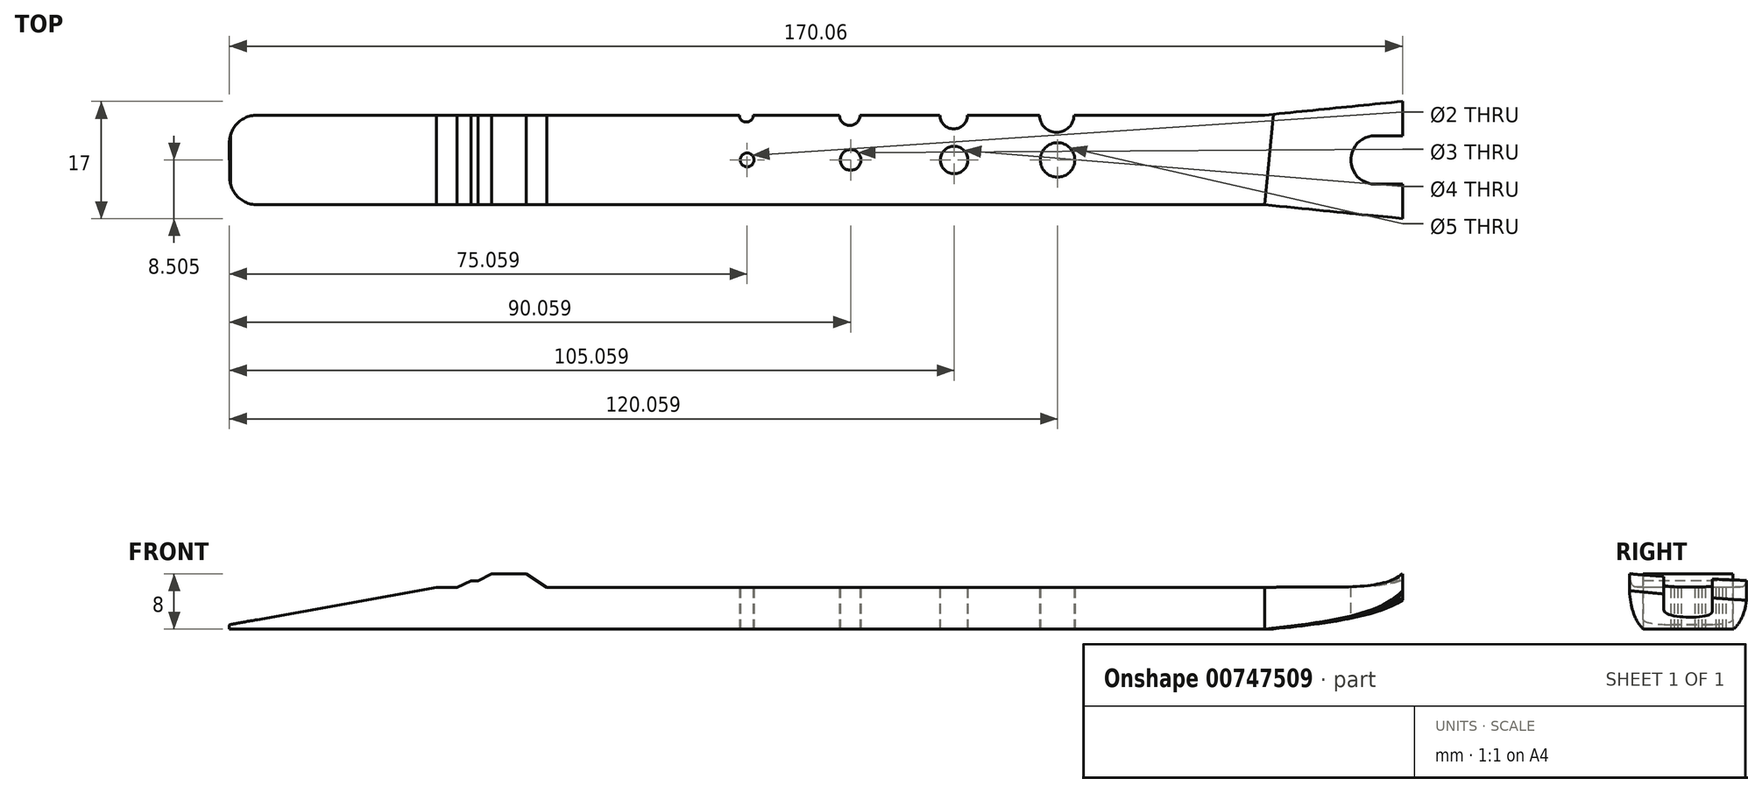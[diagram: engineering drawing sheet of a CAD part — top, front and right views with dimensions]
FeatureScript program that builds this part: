
annotation { "Feature Type Name" : "Feature", "Feature Type Description" : "" }
export const myFeature = defineFeature(function(context is Context, id is Id, definition is map)
    precondition{}
    {
        {
            var Q0;
            Q0=qCreatedBy(makeId("Top.planeOp"),FACE);
            var sketch = newSketch(context, id + "F0", { "sketchPlane" : qUnion([Q0])});
            skLineSegment(sketch, "E0", {"start": v(-98.1, -25.9) * mm, "end": v(47.93, -25.9) * mm});
            skLineSegment(sketch, "E1", {"start": v(47.93, -25.9) * mm, "end": v(47.93, -12.9) * mm});
            skLineSegment(sketch, "E2", {"start": v(47.93, -12.9) * mm, "end": v(20.3, -12.9) * mm});
            skCircle(sketch, "E3", {"center": v(-27.07, -19.4) * mm, "radius": 1 * mm});
            skCircle(sketch, "E4", {"center": v(-12.07, -19.4) * mm, "radius": 1.5 * mm});
            skCircle(sketch, "E5", {"center": v(2.93, -19.4) * mm, "radius": 2 * mm});
            skCircle(sketch, "E6", {"center": v(17.93, -19.4) * mm, "radius": 2.5 * mm});
            skArc(sketch, "E7", {"start": v(-28.2, -12.9) * mm, "mid": v(-27.2, -13.9) * mm, "end": v(-26.2, -12.9) * mm});
            skArc(sketch, "E8", {"start": v(-13.7, -12.9) * mm, "mid": v(-12.2, -14.4) * mm, "end": v(-10.7, -12.9) * mm});
            skArc(sketch, "E9", {"start": v(0.87, -12.9) * mm, "mid": v(2.87, -14.9) * mm, "end": v(4.87, -12.9) * mm});
            skArc(sketch, "E10", {"start": v(15.3, -12.9) * mm, "mid": v(17.8, -15.4) * mm, "end": v(20.3, -12.9) * mm});
            skLineSegment(sketch, "E11.trimOffspring", {"start": v(-28.2, -12.9) * mm, "end": v(-42.2, -12.9) * mm});
            skLineSegment(sketch, "E12.trimOffspring", {"start": v(-13.7, -12.9) * mm, "end": v(-26.2, -12.9) * mm});
            skLineSegment(sketch, "E13.trimOffspring", {"start": v(0.87, -12.9) * mm, "end": v(-10.7, -12.9) * mm});
            skLineSegment(sketch, "E14.trimOffspring", {"start": v(15.3, -12.9) * mm, "end": v(4.87, -12.9) * mm});
            skLineSegment(sketch, "E15", {"start": v(-42.2, -12.9) * mm, "end": v(-98.13, -12.9) * mm});
            skLineSegment(sketch, "E16", {"start": v(-42.2, -12.9) * mm, "end": v(-42.2, -25.9) * mm});
            skLineSegment(sketch, "E17", {"start": v(-102.13, -16.92) * mm, "end": v(-102.1, -21.92) * mm});
            skLineSegment(sketch, "E18", {"start": v(17.93, -19.4) * mm, "end": v(17.93, -25.9) * mm});
            skPoint(sketch, "E19.visualSharp", {"position": v(-102.16, -12.9) * mm});
            skArc(sketch, "E19.filletArc", {"start": v(-98.13, -12.9) * mm, "mid": v(-100.97, -14.07) * mm, "end": v(-102.13, -16.92) * mm});
            skPoint(sketch, "E20.visualSharp", {"position": v(-102.09, -25.9) * mm});
            skArc(sketch, "E20.filletArc", {"start": v(-102.1, -21.92) * mm, "mid": v(-100.93, -24.73) * mm, "end": v(-98.1, -25.9) * mm});
            skSolve(sketch);
        }
        {
            var Q0;
            {var subQ3=sQuery(id+"F0.wireOp",EDGE,"E1");Q0=makeQuery(id+"F0.imprint","IMPRINT",FACE,{"disambiguationData":[TD([[makeQuery(id+"F0.imprint","IMPRINT",EDGE,{"derivedFrom":subQ3}),1.0]])]});}
            var Q1;
            Q1=makeQuery(id+"F0.imprint","IMPRINT",FACE,{"disambiguationData":[TD([[makeQuery(id+"F0.imprint","IMPRINT",EDGE,{"derivedFrom":sQuery(id+"F0.wireOp",EDGE,"E15")}),1.0]])]});
            var Q2;
            Q2 = qSketchRegion(id + "F2", true);
            extrude(context, id + "F1", {"entities" : qUnion([Q0, Q1, Q2]), "depth" : 6 * mm, "offsetDistance" : 25 * mm});
        }
        {
            var Q0;
            Q0=makeQuery(id+"F1.opExtrude","CAP_FACE",FACE,{"disambiguationData":[OSD([sQuery(id+"F0.wireOp",EDGE,"uh8EjRIv-oyds-LonH-DEWT-FKtuM7sv1xbY"),sQuery(id+"F0.wireOp",EDGE,"2pE5EAkt-IuKl-0Sab-UQfI-aqEs6KhZttEm"),sQuery(id+"F0.wireOp",EDGE,"Nk6HZn5N-y9iB-Nk6B-fPmU-OZDAcxOevotu"),sQuery(id+"F0.wireOp",EDGE,"LXX49E4n-5PRi-B9FO-bH7N-pa6ycjuBgqBC"),sQuery(id+"F0.wireOp",EDGE,"53KMTElE-K7W9-ORrf-RCAp-qNT4eaaVkteF"),sQuery(id+"F0.wireOp",EDGE,"P7PF4Mbg-ef0C-n9oX-XZ09-ZLFXLgH8y7fW"),sQuery(id+"F0.wireOp",EDGE,"su197C0L-hHtV-Jca1-MSLm-PElzWjnIUR3Y"),sQuery(id+"F0.wireOp",EDGE,"EV9Pacv8-165I-bCM3-OcYT-9LR3dg5SSEyu"),sQuery(id+"F0.wireOp",EDGE,"19IYVO1Q-Y4kt-bx1a-DxFm-OXG8GlXLaGFM"),sQuery(id+"F0.wireOp",EDGE,"65VxX6mh-rfcX-KxfM-GORW-ms9ADtBnMzlR"),sQuery(id+"F0.wireOp",EDGE,"7bQUvBXv-wM8X-eBwg-Mk0h-ePabGQXhmWVm"),sQuery(id+"F0.wireOp",EDGE,"bDx1VqJG-FhMZ-ysIe-255i-NBJnI1b9v1Xd"),sQuery(id+"F0.wireOp",EDGE,"GWuhjFGg-mN8e-GpBZ-US7o-J5IPN2826qVD"),sQuery(id+"F0.wireOp",EDGE,"91LzrW2M-BcOK-ah0N-KhqT-TaDJfhBesgPh"),sQuery(id+"F0.wireOp",EDGE,"1k80qitz-qzns-NigU-Vkyj-1TzsJOIY6Jo9"),sQuery(id+"F0.wireOp",EDGE,"p5sEo6Ta-pkgy-Fa4L-bMfm-GfEhippCeM6v"),sQuery(id+"F0.wireOp",EDGE,"VcT0GBPq-V1kq-JeiP-DT5O-q3OzsVNUBB7H"),sQuery(id+"F0.wireOp",EDGE,"vWu1ZsAQ-pDto-N3AH-TT21-yHdSeIgjR8fg"),sQuery(id+"F0.wireOp",EDGE,"vBJXVKXv-qYgn-2ukd-IsI3-EiIpIBPK8Vaz"),sQuery(id+"F0.wireOp",EDGE,"G37NeImH-WY8i-Es2l-a97g-44kHUUvCxSSy"),sQuery(id+"F0.wireOp",EDGE,"E7LrDzYy-OpsH-mPZP-qLcD-qzzZRt0giBqK"),sQuery(id+"F0.wireOp",EDGE,"s3JVjWtr-fkdu-SgC5-uSSM-x588ayeuHTqY"),sQuery(id+"F0.wireOp",EDGE,"Z1yXTLh1-1L1P-RAfO-bNF2-wSMogvR3wL57"),sQuery(id+"F0.wireOp",EDGE,"ZUVO2fO2-Q0JX-bRAt-EWbK-FMEUTOadSTGL"),sQuery(id+"F0.wireOp",EDGE,"OpzXb7L7-065u-pUx9-msa7-Or2I1k12Jhel"),sQuery(id+"F0.wireOp",EDGE,"E0"),sQuery(id+"F0.wireOp",EDGE,"E1"),sQuery(id+"F0.wireOp",EDGE,"E2"),sQuery(id+"F0.wireOp",EDGE,"E3"),sQuery(id+"F0.wireOp",EDGE,"E4"),sQuery(id+"F0.wireOp",EDGE,"E5"),sQuery(id+"F0.wireOp",EDGE,"E6"),sQuery(id+"F0.wireOp",EDGE,"E7"),sQuery(id+"F0.wireOp",EDGE,"E8"),sQuery(id+"F0.wireOp",EDGE,"E9"),sQuery(id+"F0.wireOp",EDGE,"E10"),sQuery(id+"F0.wireOp",EDGE,"E11.trimOffspring"),sQuery(id+"F0.wireOp",EDGE,"E12.trimOffspring"),sQuery(id+"F0.wireOp",EDGE,"E13.trimOffspring"),sQuery(id+"F0.wireOp",EDGE,"E14.trimOffspring")])],"isStart":true});
            var sketch = newSketch(context, id + "F2", { "sketchPlane" : qUnion([Q0])});
            skLineSegment(sketch, "E21", {"start": v(47.93, 12.9) * mm, "end": v(47.93, 25.9) * mm});
            skLineSegment(sketch, "E22", {"start": v(47.93, 25.9) * mm, "end": v(67.93, 27.9) * mm});
            skLineSegment(sketch, "E23", {"start": v(47.93, 12.9) * mm, "end": v(67.93, 10.9) * mm});
            skLineSegment(sketch, "E24", {"start": v(67.93, 27.9) * mm, "end": v(67.93, 22.9) * mm});
            skLineSegment(sketch, "E25", {"start": v(67.93, 10.9) * mm, "end": v(67.93, 15.9) * mm});
            skLineSegment(sketch, "E26", {"start": v(67.93, 15.9) * mm, "end": v(63.93, 15.9) * mm});
            skLineSegment(sketch, "E27", {"start": v(67.93, 22.9) * mm, "end": v(63.93, 22.9) * mm});
            skArc(sketch, "E28", {"start": v(63.93, 15.9) * mm, "mid": v(60.43, 19.4) * mm, "end": v(63.93, 22.9) * mm});
            skSolve(sketch);
        }
        {
            var Q0;
            Q0=makeQuery(id+"F2.imprint","IMPRINT",FACE,{"disambiguationData":[TD([[makeQuery(id+"F2.imprint","IMPRINT",EDGE,{"derivedFrom":sQuery(id+"F2.wireOp",EDGE,"E21")}),1.0]])]});
            extrude(context, id + "F3", {"entities" : qUnion([Q0]), "operationType" : NewBodyOperationType.ADD, "oppositeDirection" : true, "depth" : 8 * mm, "offsetDistance" : 25 * mm});
        }
        {
            var Q0;
            Q0=makeQuery(id+"F3.opExtrude","SWEPT_FACE",FACE,{"disambiguationData":[OSD([sQuery(id+"F2.wireOp",EDGE,"E22")])]});
            var sketch = newSketch(context, id + "F4", { "sketchPlane" : qUnion([Q0])});
            skFitSpline(sketch, "E29", {"points": [v(50.27, 6) * mm, v(70.37, 8) * mm, v(72.3, 17.02) * mm], "startDerivative": vector(42.2, 1.96) * mm, "endDerivative": vector(-0.97, 25.63) * mm});
            skFitSpline(sketch, "E30", {"points": [v(50.27, 0) * mm, v(70.37, 5.57) * mm, v(72.3, 17.02) * mm], "startDerivative": vector(43.85, 4.84) * mm, "endDerivative": vector(-2.02, 30.43) * mm});
            skLineSegment(sketch, "E31", {"start": v(50.27, 21.53) * mm, "end": v(74.87, 21.53) * mm});
            skLineSegment(sketch, "E32", {"start": v(74.87, 21.53) * mm, "end": v(74.87, -3.93) * mm});
            skLineSegment(sketch, "E33", {"start": v(74.87, -3.93) * mm, "end": v(50.27, -3.93) * mm});
            skLineSegment(sketch, "E34", {"start": v(50.27, -3.93) * mm, "end": v(50.27, 0) * mm});
            skLineSegment(sketch, "E35", {"start": v(50.27, 6) * mm, "end": v(47.71, 6) * mm});
            skLineSegment(sketch, "E36", {"start": v(47.71, 6) * mm, "end": v(47.71, 21.53) * mm});
            skLineSegment(sketch, "E37", {"start": v(47.71, 21.53) * mm, "end": v(50.27, 21.53) * mm});
            skSolve(sketch);
        }
        {
            var Q0;
            Q0=makeQuery(id+"F4.imprint","IMPRINT",FACE,{"disambiguationData":[TD([[makeQuery(id+"F4.imprint","IMPRINT",EDGE,{"derivedFrom":sQuery(id+"F4.wireOp",EDGE,"E31")}),-1.0]])]});
            var Q1;
            {var subQ1=sQuery(id+"F2.wireOp",EDGE,"E22");var subQ2=makeQuery(id+"F3.opExtrude","CAP_EDGE",EDGE,{"disambiguationData":[OSD([subQ1])],"isStart":false});Q1=makeQuery(id+"F4.imprint","IMPRINT",FACE,{"disambiguationData":[TD([[makeQuery(id+"F4.imprint","IMPRINT",EDGE,{"derivedFrom":subQ2}),-1.0]])]});}
            var Q2;
            {var subQ1=sQuery(id+"F2.wireOp",EDGE,"E22");var subQ3=makeQuery(id+"F3.opExtrude","CAP_EDGE",EDGE,{"disambiguationData":[OSD([subQ1])],"isStart":true});Q2=makeQuery(id+"F4.imprint","IMPRINT",FACE,{"disambiguationData":[TD([[makeQuery(id+"F4.imprint","IMPRINT",EDGE,{"derivedFrom":subQ3}),1.0]])]});}
            extrude(context, id + "F5", {"entities" : qUnion([Q0, Q1, Q2]), "operationType" : NewBodyOperationType.REMOVE, "oppositeDirection" : true, "depth" : 25 * mm, "offsetDistance" : 25 * mm});
        }
        {
            var Q0;
            Q0=makeQuery(id+"F1.opExtrude","SWEPT_FACE",FACE,{"disambiguationData":[OSD([sQuery(id+"F0.wireOp",EDGE,"E0")])]});
            var sketch = newSketch(context, id + "F6", { "sketchPlane" : qUnion([Q0])});
            skLineSegment(sketch, "E38", {"start": v(-98.1, 0) * mm, "end": v(-102.1, 0) * mm});
            skLineSegment(sketch, "E39", {"start": v(-98.1, 0) * mm, "end": v(-72.1, 0) * mm});
            skLineSegment(sketch, "E40", {"start": v(-72.1, 0) * mm, "end": v(-72.1, 6) * mm});
            skLineSegment(sketch, "E41", {"start": v(-102.1, 0) * mm, "end": v(-102.1, 0.5) * mm});
            skLineSegment(sketch, "E42", {"start": v(-101.98, 0.65) * mm, "end": v(-72.1, 6) * mm});
            skLineSegment(sketch, "E43", {"start": v(-72.1, 6) * mm, "end": v(-72.1, 8.95) * mm});
            skLineSegment(sketch, "E44", {"start": v(-72.1, 8.95) * mm, "end": v(-103.5, 6.68) * mm});
            skLineSegment(sketch, "E45", {"start": v(-103.5, 6.68) * mm, "end": v(-103.67, 0) * mm});
            skLineSegment(sketch, "E46", {"start": v(-103.67, 0) * mm, "end": v(-101.98, 0.65) * mm});
            skSolve(sketch);
        }
        {
            var Q0;
            Q0 = qSketchRegion(id + "F6", true);
            extrude(context, id + "F7", {"entities" : qUnion([Q0]), "operationType" : NewBodyOperationType.REMOVE, "oppositeDirection" : true, "depth" : 25 * mm, "offsetDistance" : 25 * mm});
        }
        {
            var Q0;
            Q0=makeQuery(id+"F1.opExtrude","SWEPT_FACE",FACE,{"disambiguationData":[OSD([sQuery(id+"F0.wireOp",EDGE,"E0")])]});
            var sketch = newSketch(context, id + "F8", { "sketchPlane" : qUnion([Q0])});
            skLineSegment(sketch, "E47", {"start": v(-69.1, 6) * mm, "end": v(-67.1, 6) * mm});
            skLineSegment(sketch, "E48", {"start": v(-67.1, 7) * mm, "end": v(-66.1, 7) * mm});
            skLineSegment(sketch, "E49", {"start": v(-56.1, 6) * mm, "end": v(-67.1, 6) * mm});
            skLineSegment(sketch, "E50", {"start": v(-69.1, 6) * mm, "end": v(-67.1, 7) * mm});
            skLineSegment(sketch, "E51", {"start": v(-66.1, 7) * mm, "end": v(-64.1, 7) * mm, "construction": true});
            skLineSegment(sketch, "E52", {"start": v(-64.1, 7) * mm, "end": v(-64.1, 8) * mm, "construction": true});
            skLineSegment(sketch, "E53", {"start": v(-66.1, 7) * mm, "end": v(-64.1, 8) * mm});
            skLineSegment(sketch, "E54", {"start": v(-64.1, 8) * mm, "end": v(-59.1, 8) * mm});
            skLineSegment(sketch, "E55", {"start": v(-59.1, 8) * mm, "end": v(-56.1, 6) * mm});
            skSolve(sketch);
        }
        {
            var Q0;
            Q0=makeQuery(id+"F8.imprint","IMPRINT",FACE,{"disambiguationData":[TD([[makeQuery(id+"F8.imprint","IMPRINT",EDGE,{"derivedFrom":sQuery(id+"F8.wireOp",EDGE,"E47")}),1.0]])]});
            extrude(context, id + "F9", {"entities" : qUnion([Q0]), "operationType" : NewBodyOperationType.ADD, "oppositeDirection" : true, "depth" : 13 * mm, "offsetDistance" : 25 * mm});
        }
    });
